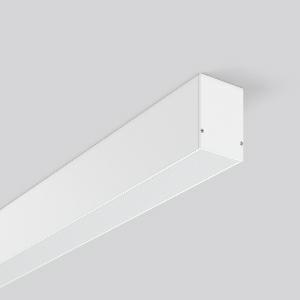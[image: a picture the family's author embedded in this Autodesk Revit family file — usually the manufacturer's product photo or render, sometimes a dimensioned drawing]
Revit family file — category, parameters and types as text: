
# Revit family: less_is_more_50_312307_002_7268
name_source: partatom
category: Lighting Fixtures
units: mm (PartAtom-declared; Revit-internal decimal feet)

## family parameters
Cut with Voids When Loaded = No
Host = Face
Light Source = No
Part Type = Normal
Room Calculation Point = No
Round Connector Dimension = Use Diameter
Shared = No

## types (1)
- LESS IS MORE 50 (1 x LED Modul 830, 3850 lm, 3000)
    Apparent Load = 34 VA
    CIE Flux Codes = 48 79 95 100 100
    Color Rendering = 80
    Color Temperature = 3000
    Default Elevation = 1800 mm
    Description = Series: LESS IS MORE 50
Linear ceiling and wall luminaire for aesthetically sophisticated lighting. Housing: extruded aluminium profile, powder-coated. End cap aluminium powder-coated. Diffuser made of non-yellowing plastic (PMMA), opal. Suitable for Ceiling mounting. LED unit with integrated converter interchangeable and removable. Suitable for through-wiring. With sensors or as a safety luminaire on request. 
Colour: traffic white, matt (RAL 9016)
Length: 1407 mm
Width: 57 mm
Height: 75 mm
Lamp: LED
Socket: without socket
Colour temperature: 3000K
Colour rendering index (CRI): 80
System power: 34 W
Rated luminous flux: 3850 lm
Luminous efficiency: 113 lm/W
Control gear: Regulated power supply
Protection class: I
Type of protection: IP 20
    Height = 75 mm
    Lamp = 1 x LED Modul 830
    Lamp Light Flux = 3850 lm
    Lamp count = 1
    Length = 1407 mm
    Lifetime = 50000 h
    Luminous efficacy = 113 lm/W
    Manufacturer = RZB
    ModVariant = No
    Model = 312307.002
    Mounting Place = Ceiling
    Mounting Type = Surface mounted
    Number of Poles = 1
    OnlyDefault = Yes
    Power Factor = 1
    Product Name = LESS IS MORE 50
    Product group = Surface mounted ceiling LED linear luminaires
    ProductGroupID = 312
    Protection Class = Protection class I
    Protection Degree = IP 20
    RLX_Detail_Level = 1
    RLX_Emergency_Light_Flux = 0 lm
    RLX_Emergency_Type = 0
    RLX_Emergency_Type_DB = No
    RlxData = <blob elided: 21393 chars, md5=54b4a7a3>
    Socket = socket
    Standby Power = 0 W
    System Light Flux = 3850 lm
    System Power = 34 W
    Type Comments = Product without accessories
    Type Image = 312306.002.jpg
    URL = http://relux.com
    VarID = ---
    Voltage = 230 V
    Voltage Range = 220-240 V
    Weight = 0.00 kg
    Width = 57 mm

## geometry (parser evidence)
native form markers: Blend x4, Sweep x12
no freeform markers — native parametric forms only
